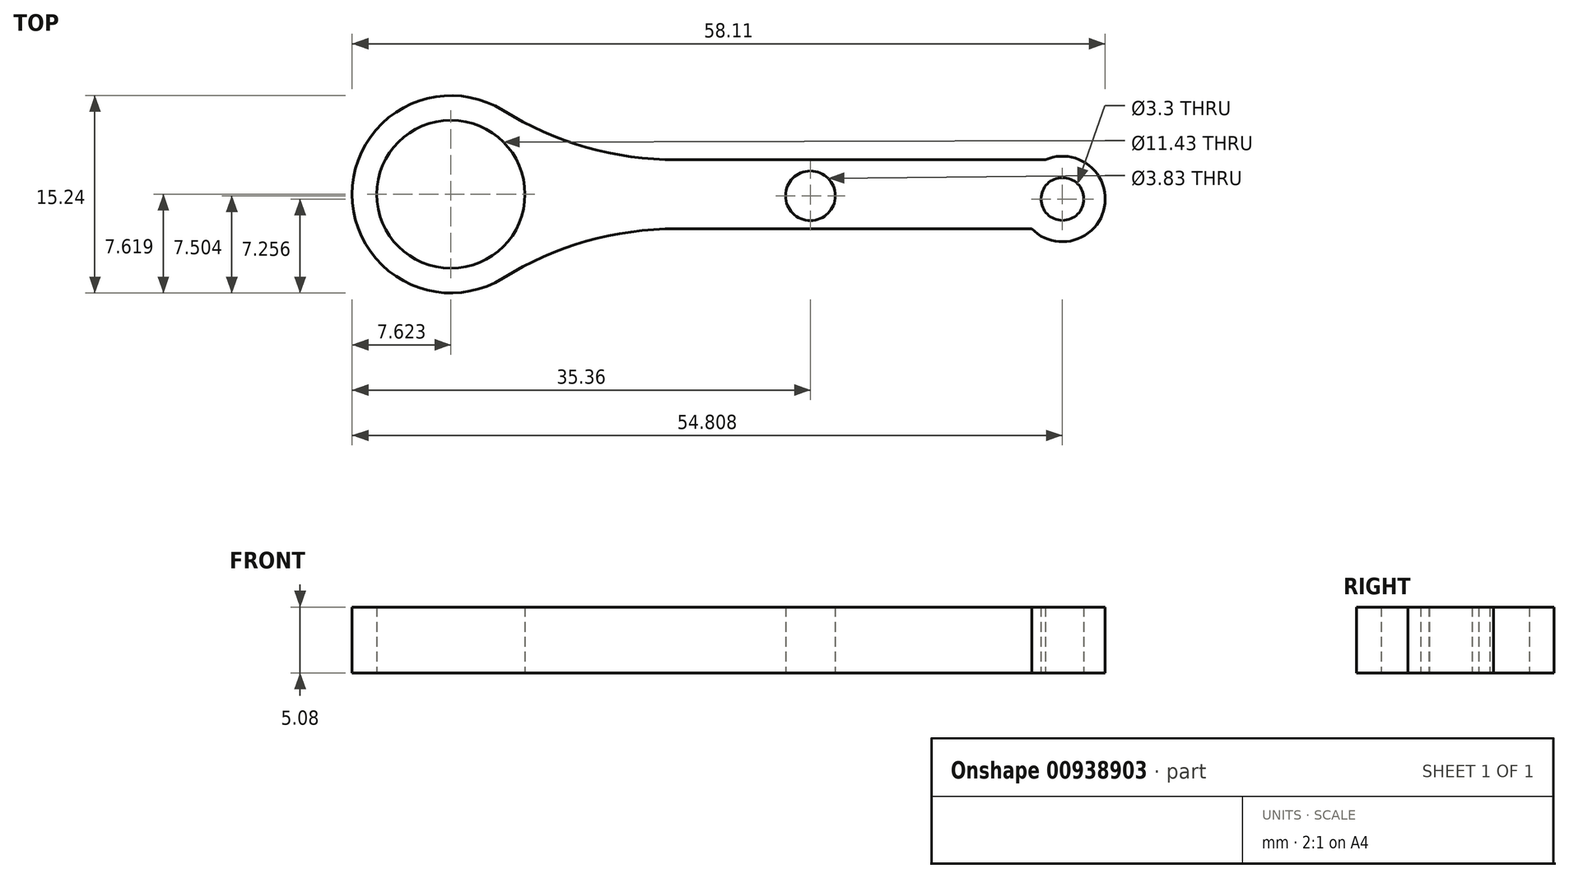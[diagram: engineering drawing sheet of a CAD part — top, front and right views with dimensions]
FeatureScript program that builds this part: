
annotation { "Feature Type Name" : "Feature", "Feature Type Description" : "" }
export const myFeature = defineFeature(function(context is Context, id is Id, definition is map)
    precondition{}
    {
        {
            var Q0;
            Q0=qCreatedBy(makeId("Top.planeOp"),FACE);
            var sketch = newSketch(context, id + "F0", { "sketchPlane" : qUnion([Q0])});
            skLineSegment(sketch, "E0", {"start": v(-10.33, 0) * mm, "end": v(17.07, 0) * mm});
            skLineSegment(sketch, "E1", {"start": v(-10.33, 5.32) * mm, "end": v(18.12, 5.32) * mm});
            skArc(sketch, "E2", {"start": v(-23.72, 9.13) * mm, "mid": v(-35.36, 2.66) * mm, "end": v(-23.72, -3.82) * mm});
            skArc(sketch, "E3", {"start": v(17.07, 0) * mm, "mid": v(22.69, 1.66) * mm, "end": v(18.12, 5.32) * mm});
            skCircle(sketch, "E4", {"center": v(-27.74, 2.66) * mm, "radius": 5.72 * mm});
            skCircle(sketch, "E5", {"center": v(19.45, 2.3) * mm, "radius": 1.65 * mm});
            skArc(sketch, "E6.filletArc", {"start": v(-23.72, 9.13) * mm, "mid": v(-17.3, 6.3) * mm, "end": v(-10.33, 5.32) * mm});
            skArc(sketch, "E7.filletArc", {"start": v(-10.33, 0) * mm, "mid": v(-17.3, -0.97) * mm, "end": v(-23.72, -3.82) * mm});
            skCircle(sketch, "E8", {"center": v(0, 2.54) * mm, "radius": 1.92 * mm});
            skSolve(sketch);
        }
        {
            var Q0;
            Q0 = qSketchRegion(id + "F0", true);
            extrude(context, id + "F1", {"entities" : qUnion([Q0]), "depth" : 5.08 * mm, "offsetDistance" : 25.4 * mm});
        }
    });
